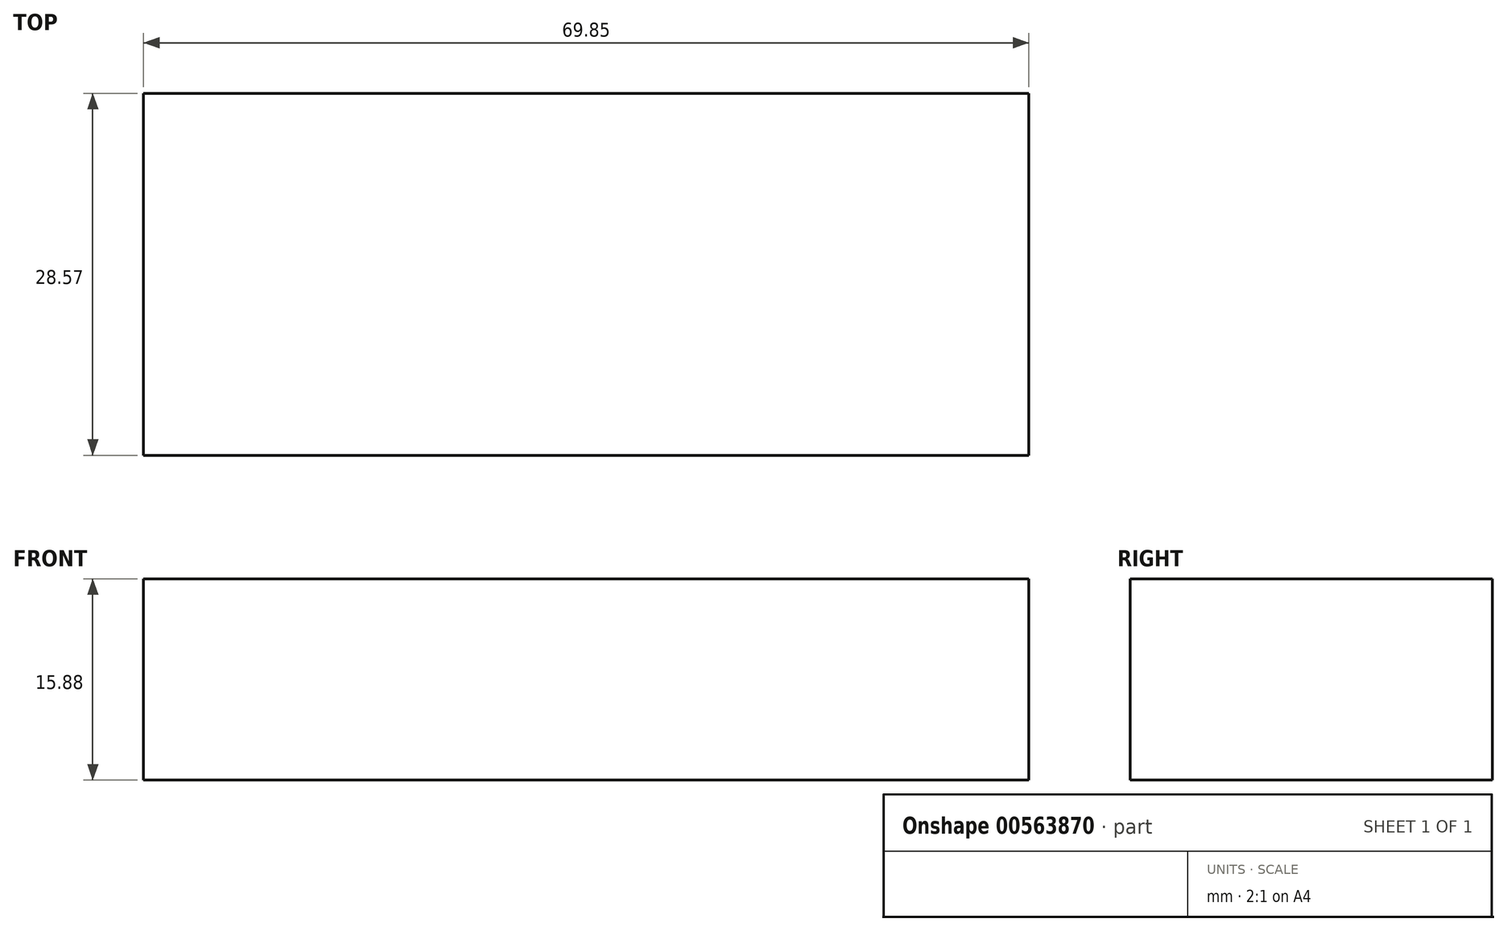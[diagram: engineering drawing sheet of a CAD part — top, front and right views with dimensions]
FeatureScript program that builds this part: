
annotation { "Feature Type Name" : "Feature", "Feature Type Description" : "" }
export const myFeature = defineFeature(function(context is Context, id is Id, definition is map)
    precondition{}
    {
        {
            var Q0;
            Q0=qCreatedBy(makeId("Top.planeOp"),FACE);
            var sketch = newSketch(context, id + "F0", { "sketchPlane" : qUnion([Q0])});
            skLineSegment(sketch, "E0.bottom", {"start": v(0, 0) * mm, "end": v(69.85, 0) * mm});
            skLineSegment(sketch, "E0.top", {"start": v(0, 28.57) * mm, "end": v(69.85, 28.57) * mm});
            skLineSegment(sketch, "E0.left", {"start": v(0, 0) * mm, "end": v(0, 28.57) * mm});
            skLineSegment(sketch, "E0.right", {"start": v(69.85, 0) * mm, "end": v(69.85, 28.57) * mm});
            skSolve(sketch);
        }
        {
            var Q0;
            Q0=makeQuery(id+"F0.imprint","IMPRINT",FACE,{"disambiguationData":[TD([[makeQuery(id+"F0.imprint","IMPRINT",EDGE,{"derivedFrom":sQuery(id+"F0.wireOp",EDGE,"E0.bottom")}),1.0]])]});
            extrude(context, id + "F1", {"entities" : qUnion([Q0]), "depth" : 15.88 * mm, "offsetDistance" : 25.4 * mm});
        }
    });
